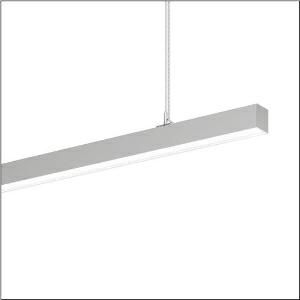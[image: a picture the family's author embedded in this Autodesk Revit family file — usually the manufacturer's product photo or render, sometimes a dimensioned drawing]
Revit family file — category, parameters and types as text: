
# Revit family: silica_r__21_51mx30da34sb_350b
name_source: partatom
category: Lighting Fixtures
units: mm (PartAtom-declared; Revit-internal decimal feet)

## family parameters
Cut with Voids When Loaded = No
Host = Face
Light Source = No
Part Type = Normal
Room Calculation Point = No
Round Connector Dimension = Use Diameter
Shared = No

## types (1)
- --- (1 x LED, 4210 lm, 27.7 W, 3000K)
    Apparent Load = 28 VA
    CIE Flux Codes = 47 79 96 57 100
    Color Rendering = 80
    Color Temperature = 3000K
    Default Elevation = 1800 mm
    Description = Silica® 21, office luminaire, primary optical cover: cover, of PMMA, opal, light emission: direct/indirect distribution, primary light characteristic: symmetric, installation type: suspended mounting, LED, rated luminous flux: 4.210lm, luminous efficacy: 152lm/W, light colour: 830, colour temperature: 3000K, with terminal, 3+2-pole, max. 2.5mm², mains connection: 220..240V, AC, 50/60Hz, rated input power: 27.7W, luminaire housing, of aluminium, metallic grey (RAL 9006), length: 1.204mm, width: 53mm, height: 53mm, protection rating (complete): IP20, insulation class (complete): insulation class I (protective earthing), certification: CE, permissible operating ambient temperature: 0..+35°C, standard: EN 50419, packaging unit: 1 piece
    Height = 53 mm
    Lamp = 1 x LED
    Lamp Light Flux = 4210 lm
    Lamp Power = 27.7 W
    Lamp count = 1
    Length = 1204 mm
    Luminous efficacy = 152 lm/W
    Manufacturer = Siteco
    ModVariant = No
    Model = 51MX30DA34SB
    Mounting Place = Ceiling
    Mounting Type = Pendant
    Number of Poles = 1
    OnlyDefault = Yes
    Power Factor = 1
    Product Name = Silica® 21
    Product group = office luminaire | ceiling pendant
    ProductGroupID = 902
    Protection Class = Protection class I
    Protection Degree = IP 20
    RLX_Detail_Level = 1
    RLX_Emergency_Light_Flux = 0 lm
    RLX_Emergency_Type = 0
    RLX_Emergency_Type_DB = No
    RlxData = <blob elided: 23193 chars, md5=5d0dc12f>
    Socket = socket
    Standby Power = 0 W
    System Light Flux = 4210 lm
    System Power = 28 W
    Type Comments = factory setting: luminous flux: 100 % | dim-lin: 254 | 233 mA
    Type Image = l_1313621.jpg
    URL = http://relux.com
    VarID = @adj_065343
    Voltage = 0 V
    Weight = 0.00 kg
    Width = 53 mm

## geometry (parser evidence)
native form markers: Blend x4, Sweep x12
no freeform markers — native parametric forms only
